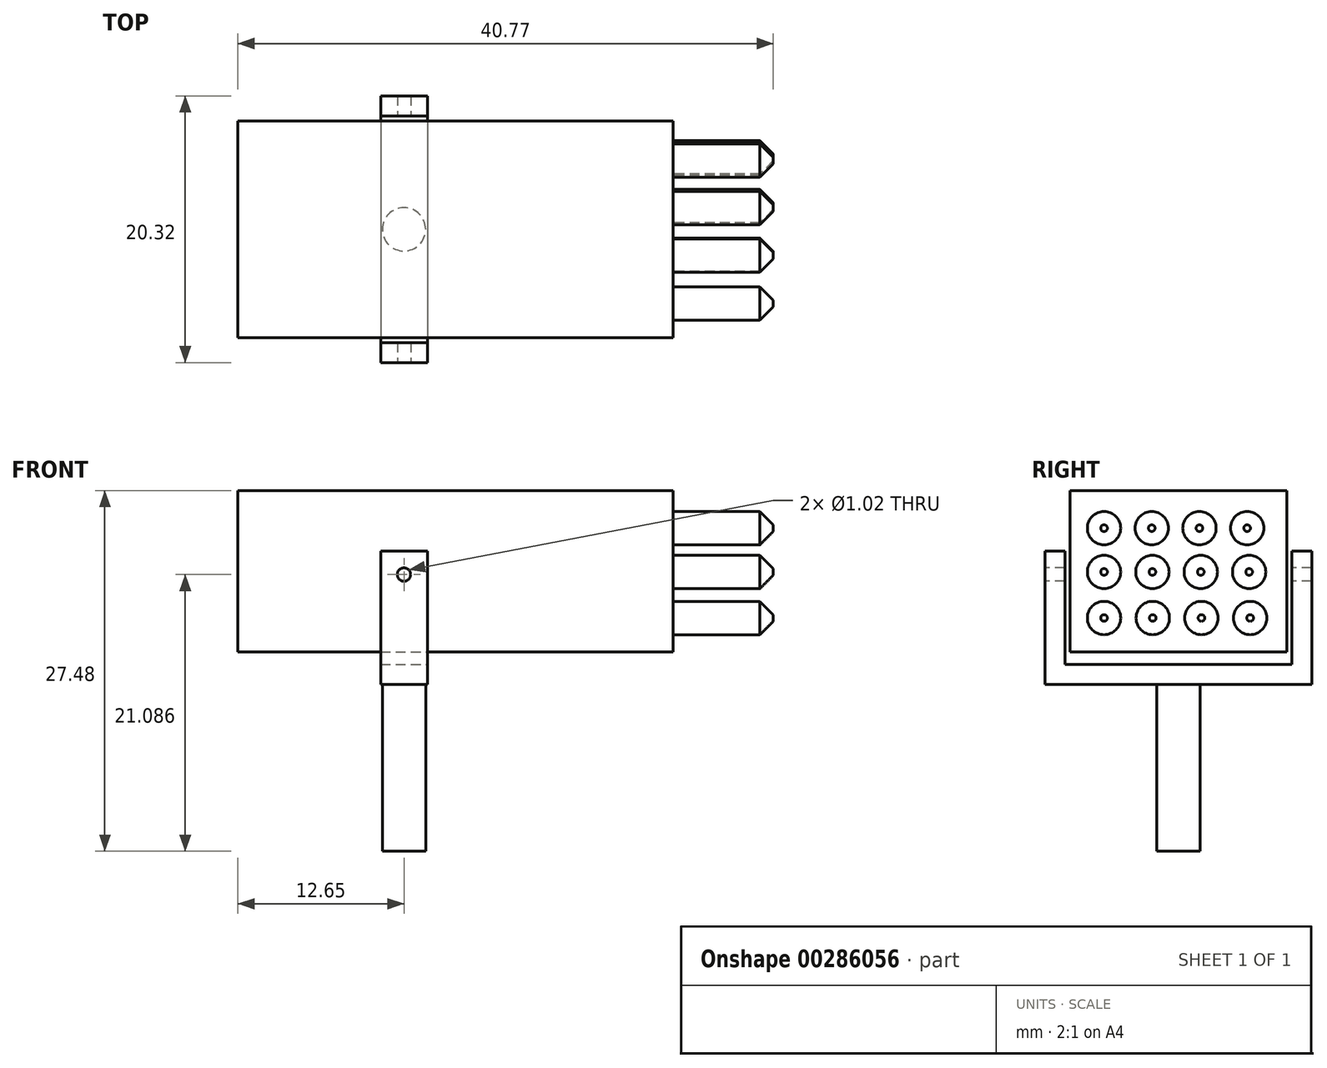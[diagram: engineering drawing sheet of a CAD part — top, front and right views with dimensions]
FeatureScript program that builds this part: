
annotation { "Feature Type Name" : "Feature", "Feature Type Description" : "" }
export const myFeature = defineFeature(function(context is Context, id is Id, definition is map)
    precondition{}
    {
        {
            var Q0;
            Q0=qCreatedBy(makeId("Top.planeOp"),FACE);
            var sketch = newSketch(context, id + "F0", { "sketchPlane" : qUnion([Q0])});
            skCircle(sketch, "E0", {"center": v(0, 0) * mm, "radius": 1.65 * mm});
            skLineSegment(sketch, "E1.bottom", {"start": v(-1.78, 10.16) * mm, "end": v(1.78, 10.16) * mm});
            skLineSegment(sketch, "E1.top", {"start": v(-1.78, -10.16) * mm, "end": v(1.78, -10.16) * mm});
            skLineSegment(sketch, "E1.left", {"start": v(-1.78, 10.16) * mm, "end": v(-1.78, -10.16) * mm});
            skLineSegment(sketch, "E1.right", {"start": v(1.78, 10.16) * mm, "end": v(1.78, -10.16) * mm});
            skLineSegment(sketch, "E2.top", {"start": v(-1.78, 8.64) * mm, "end": v(1.78, 8.64) * mm});
            skLineSegment(sketch, "E2.left", {"start": v(-1.78, 10.16) * mm, "end": v(-1.78, 8.64) * mm});
            skLineSegment(sketch, "E2.right", {"start": v(1.78, 10.16) * mm, "end": v(1.78, 8.64) * mm});
            skLineSegment(sketch, "E3.top", {"start": v(-1.78, -8.64) * mm, "end": v(1.78, -8.64) * mm});
            skLineSegment(sketch, "E3.left", {"start": v(-1.78, -10.16) * mm, "end": v(-1.78, -8.64) * mm});
            skLineSegment(sketch, "E3.right", {"start": v(1.78, -10.16) * mm, "end": v(1.78, -8.64) * mm});
            skSolve(sketch);
        }
        {
            var Q0;
            Q0=makeQuery(id+"F0.imprint","IMPRINT",FACE,{"disambiguationData":[TD([[makeQuery(id+"F0.imprint","IMPRINT",EDGE,{"derivedFrom":sQuery(id+"F0.wireOp",EDGE,"E0")}),1.0]])]});
            extrude(context, id + "F1", {"entities" : qUnion([Q0]), "oppositeDirection" : true, "depth" : 12.7 * mm});
        }
        {
            var Q0;
            Q0=makeQuery(id+"F0.imprint","IMPRINT",FACE,{"disambiguationData":[TD([[makeQuery(id+"F0.imprint","IMPRINT",EDGE,{"derivedFrom":sQuery(id+"F0.wireOp",EDGE,"E0")}),1.0]])]});
            var Q1;
            Q1=makeQuery(id+"F0.imprint","IMPRINT",FACE,{"disambiguationData":[TD([[makeQuery(id+"F0.imprint","IMPRINT",EDGE,{"derivedFrom":sQuery(id+"F0.wireOp",EDGE,"E0")}),-1.0]])]});
            extrude(context, id + "F2", {"entities" : qUnion([Q0, Q1]), "operationType" : NewBodyOperationType.ADD, "depth" : 1.52 * mm});
        }
        {
            var Q0;
            Q0=makeQuery(id+"F0.imprint","IMPRINT",FACE,{"disambiguationData":[TD([[makeQuery(id+"F0.imprint","IMPRINT",EDGE,{"derivedFrom":sQuery(id+"F0.wireOp",EDGE,"E1.bottom")}),-1.0]])]});
            var Q1;
            Q1=makeQuery(id+"F0.imprint","IMPRINT",FACE,{"disambiguationData":[TD([[makeQuery(id+"F0.imprint","IMPRINT",EDGE,{"derivedFrom":sQuery(id+"F0.wireOp",EDGE,"E1.top")}),1.0]])]});
            extrude(context, id + "F3", {"entities" : qUnion([Q0, Q1]), "operationType" : NewBodyOperationType.ADD, "depth" : 10.16 * mm});
        }
        {
            var Q0;
            Q0=makeQuery(id+"F3.opExtrude","SWEPT_FACE",FACE,{"disambiguationData":[OSD([sQuery(id+"F0.wireOp",EDGE,"E1.top")])]});
            var sketch = newSketch(context, id + "F4", { "sketchPlane" : qUnion([Q0])});
            skCircle(sketch, "E4", {"center": v(0, 8.39) * mm, "radius": 0.5 * mm});
            skSolve(sketch);
        }
        {
            var Q0;
            Q0=makeQuery(id+"F4.imprint","IMPRINT",FACE,{"disambiguationData":[TD([[makeQuery(id+"F4.imprint","IMPRINT",EDGE,{"derivedFrom":sQuery(id+"F4.wireOp",EDGE,"E4")}),1.0]])]});
            extrude(context, id + "F5", {"entities" : qUnion([Q0]), "operationType" : NewBodyOperationType.REMOVE, "endBound" : BoundingType.SYMMETRIC, "oppositeDirection" : true, "depth" : 53.14 * mm});
        }
        {
            var Q0;
            Q0=qCreatedBy(makeId("Front.planeOp"),FACE);
            var sketch = newSketch(context, id + "F6", { "sketchPlane" : qUnion([Q0])});
            skLineSegment(sketch, "E5.bottom", {"start": v(-12.65, 2.48) * mm, "end": v(20.5, 2.48) * mm});
            skLineSegment(sketch, "E5.top", {"start": v(-12.65, 14.78) * mm, "end": v(20.5, 14.78) * mm});
            skLineSegment(sketch, "E5.left", {"start": v(-12.65, 2.48) * mm, "end": v(-12.65, 14.78) * mm});
            skLineSegment(sketch, "E5.right", {"start": v(20.5, 2.48) * mm, "end": v(20.5, 14.78) * mm});
            skSolve(sketch);
        }
        {
            var Q0;
            Q0=makeQuery(id+"F6.imprint","IMPRINT",FACE,{"disambiguationData":[TD([[makeQuery(id+"F6.imprint","IMPRINT",EDGE,{"derivedFrom":sQuery(id+"F6.wireOp",EDGE,"E5.bottom")}),1.0]])]});
            extrude(context, id + "F7", {"entities" : qUnion([Q0]), "endBound" : BoundingType.SYMMETRIC, "depth" : 16.5 * mm});
        }
        {
            var Q0;
            Q0=makeQuery(id+"F7.opExtrude","SWEPT_FACE",FACE,{"disambiguationData":[OSD([sQuery(id+"F6.wireOp",EDGE,"E5.right")])]});
            var sketch = newSketch(context, id + "F8", { "sketchPlane" : qUnion([Q0])});
            skCircle(sketch, "E6", {"center": v(-5.65, 11.92) * mm, "radius": 1.27 * mm});
            skCircle(sketch, "E7", {"center": v(-5.65, 8.58) * mm, "radius": 1.27 * mm});
            skCircle(sketch, "E8", {"center": v(-5.65, 5.08) * mm, "radius": 1.27 * mm});
            skCircle(sketch, "E9.1.0.0", {"center": v(-2.02, 11.92) * mm, "radius": 1.27 * mm});
            skCircle(sketch, "E9.2.0.0", {"center": v(1.61, 11.92) * mm, "radius": 1.27 * mm});
            skCircle(sketch, "E9.3.0.0", {"center": v(5.25, 11.92) * mm, "radius": 1.27 * mm});
            skLineSegment(sketch, "E9.direction1", {"start": v(-5.65, 11.92) * mm, "end": v(-2.02, 11.92) * mm, "construction": true});
            skCircle(sketch, "E10.1.0.0", {"center": v(-1.97, 8.58) * mm, "radius": 1.27 * mm});
            skCircle(sketch, "E10.2.0.0", {"center": v(1.72, 8.58) * mm, "radius": 1.27 * mm});
            skCircle(sketch, "E10.3.0.0", {"center": v(5.4, 8.58) * mm, "radius": 1.27 * mm});
            skLineSegment(sketch, "E10.direction1", {"start": v(-5.65, 8.58) * mm, "end": v(-1.97, 8.58) * mm, "construction": true});
            skCircle(sketch, "E11.1.0.0", {"center": v(-1.94, 5.08) * mm, "radius": 1.27 * mm});
            skCircle(sketch, "E11.2.0.0", {"center": v(1.77, 5.08) * mm, "radius": 1.27 * mm});
            skCircle(sketch, "E11.3.0.0", {"center": v(5.47, 5.08) * mm, "radius": 1.27 * mm});
            skLineSegment(sketch, "E11.direction1", {"start": v(-5.65, 5.08) * mm, "end": v(-1.94, 5.08) * mm, "construction": true});
            skSolve(sketch);
        }
        {
            var Q0;
            Q0=makeQuery(id+"F8.imprint","IMPRINT",FACE,{"disambiguationData":[TD([[makeQuery(id+"F8.imprint","IMPRINT",EDGE,{"derivedFrom":sQuery(id+"F8.wireOp",EDGE,"E6")}),1.0]])]});
            var Q1;
            Q1=makeQuery(id+"F8.imprint","IMPRINT",FACE,{"disambiguationData":[TD([[makeQuery(id+"F8.imprint","IMPRINT",EDGE,{"derivedFrom":sQuery(id+"F8.wireOp",EDGE,"E9.1.0.0")}),1.0]])]});
            var Q2;
            Q2=makeQuery(id+"F8.imprint","IMPRINT",FACE,{"disambiguationData":[TD([[makeQuery(id+"F8.imprint","IMPRINT",EDGE,{"derivedFrom":sQuery(id+"F8.wireOp",EDGE,"E9.2.0.0")}),1.0]])]});
            var Q3;
            Q3=makeQuery(id+"F8.imprint","IMPRINT",FACE,{"disambiguationData":[TD([[makeQuery(id+"F8.imprint","IMPRINT",EDGE,{"derivedFrom":sQuery(id+"F8.wireOp",EDGE,"E9.3.0.0")}),1.0]])]});
            var Q4;
            Q4=makeQuery(id+"F8.imprint","IMPRINT",FACE,{"disambiguationData":[TD([[makeQuery(id+"F8.imprint","IMPRINT",EDGE,{"derivedFrom":sQuery(id+"F8.wireOp",EDGE,"E10.3.0.0")}),1.0]])]});
            var Q5;
            Q5=makeQuery(id+"F8.imprint","IMPRINT",FACE,{"disambiguationData":[TD([[makeQuery(id+"F8.imprint","IMPRINT",EDGE,{"derivedFrom":sQuery(id+"F8.wireOp",EDGE,"E11.3.0.0")}),1.0]])]});
            var Q6;
            Q6=makeQuery(id+"F8.imprint","IMPRINT",FACE,{"disambiguationData":[TD([[makeQuery(id+"F8.imprint","IMPRINT",EDGE,{"derivedFrom":sQuery(id+"F8.wireOp",EDGE,"E11.2.0.0")}),1.0]])]});
            var Q7;
            Q7=makeQuery(id+"F8.imprint","IMPRINT",FACE,{"disambiguationData":[TD([[makeQuery(id+"F8.imprint","IMPRINT",EDGE,{"derivedFrom":sQuery(id+"F8.wireOp",EDGE,"E10.2.0.0")}),1.0]])]});
            var Q8;
            Q8=makeQuery(id+"F8.imprint","IMPRINT",FACE,{"disambiguationData":[TD([[makeQuery(id+"F8.imprint","IMPRINT",EDGE,{"derivedFrom":sQuery(id+"F8.wireOp",EDGE,"E10.1.0.0")}),1.0]])]});
            var Q9;
            Q9=makeQuery(id+"F8.imprint","IMPRINT",FACE,{"disambiguationData":[TD([[makeQuery(id+"F8.imprint","IMPRINT",EDGE,{"derivedFrom":sQuery(id+"F8.wireOp",EDGE,"E11.1.0.0")}),1.0]])]});
            var Q10;
            Q10=makeQuery(id+"F8.imprint","IMPRINT",FACE,{"disambiguationData":[TD([[makeQuery(id+"F8.imprint","IMPRINT",EDGE,{"derivedFrom":sQuery(id+"F8.wireOp",EDGE,"E7")}),1.0]])]});
            var Q11;
            Q11=makeQuery(id+"F8.imprint","IMPRINT",FACE,{"disambiguationData":[TD([[makeQuery(id+"F8.imprint","IMPRINT",EDGE,{"derivedFrom":sQuery(id+"F8.wireOp",EDGE,"E8")}),1.0]])]});
            extrude(context, id + "F9", {"entities" : qUnion([Q0, Q1, Q2, Q3, Q4, Q5, Q6, Q7, Q8, Q9, Q10, Q11]), "operationType" : NewBodyOperationType.ADD, "depth" : 7.62 * mm});
        }
        {
            var Q0;
            Q0=makeQuery(id+"F9.opExtrude","CAP_EDGE",EDGE,{"disambiguationData":[OSD([sQuery(id+"F8.wireOp",EDGE,"E6")])],"isStart":false});
            var Q1;
            Q1=makeQuery(id+"F9.opExtrude","CAP_EDGE",EDGE,{"disambiguationData":[OSD([sQuery(id+"F8.wireOp",EDGE,"E9.1.0.0")])],"isStart":false});
            var Q2;
            Q2=makeQuery(id+"F9.opExtrude","CAP_EDGE",EDGE,{"disambiguationData":[OSD([sQuery(id+"F8.wireOp",EDGE,"E9.2.0.0")])],"isStart":false});
            var Q3;
            Q3=makeQuery(id+"F9.opExtrude","CAP_EDGE",EDGE,{"disambiguationData":[OSD([sQuery(id+"F8.wireOp",EDGE,"E9.3.0.0")])],"isStart":false});
            var Q4;
            Q4=makeQuery(id+"F9.opExtrude","CAP_EDGE",EDGE,{"disambiguationData":[OSD([sQuery(id+"F8.wireOp",EDGE,"E10.3.0.0")])],"isStart":false});
            var Q5;
            Q5=makeQuery(id+"F9.opExtrude","CAP_EDGE",EDGE,{"disambiguationData":[OSD([sQuery(id+"F8.wireOp",EDGE,"E10.2.0.0")])],"isStart":false});
            var Q6;
            Q6=makeQuery(id+"F9.opExtrude","CAP_EDGE",EDGE,{"disambiguationData":[OSD([sQuery(id+"F8.wireOp",EDGE,"E10.1.0.0")])],"isStart":false});
            var Q7;
            Q7=makeQuery(id+"F9.opExtrude","CAP_EDGE",EDGE,{"disambiguationData":[OSD([sQuery(id+"F8.wireOp",EDGE,"E7")])],"isStart":false});
            var Q8;
            Q8=makeQuery(id+"F9.opExtrude","CAP_EDGE",EDGE,{"disambiguationData":[OSD([sQuery(id+"F8.wireOp",EDGE,"E8")])],"isStart":false});
            var Q9;
            Q9=makeQuery(id+"F9.opExtrude","CAP_EDGE",EDGE,{"disambiguationData":[OSD([sQuery(id+"F8.wireOp",EDGE,"E11.1.0.0")])],"isStart":false});
            var Q10;
            Q10=makeQuery(id+"F9.opExtrude","CAP_EDGE",EDGE,{"disambiguationData":[OSD([sQuery(id+"F8.wireOp",EDGE,"E11.2.0.0")])],"isStart":false});
            var Q11;
            Q11=makeQuery(id+"F9.opExtrude","CAP_EDGE",EDGE,{"disambiguationData":[OSD([sQuery(id+"F8.wireOp",EDGE,"E11.3.0.0")])],"isStart":false});
            chamfer(context, id + "F10", {"entities" : qUnion([Q0, Q1, Q2, Q3, Q4, Q5, Q6, Q7, Q8, Q9, Q10, Q11]), "width" : 1.02 * mm, "tangentPropagation" : true});
        }
    });
